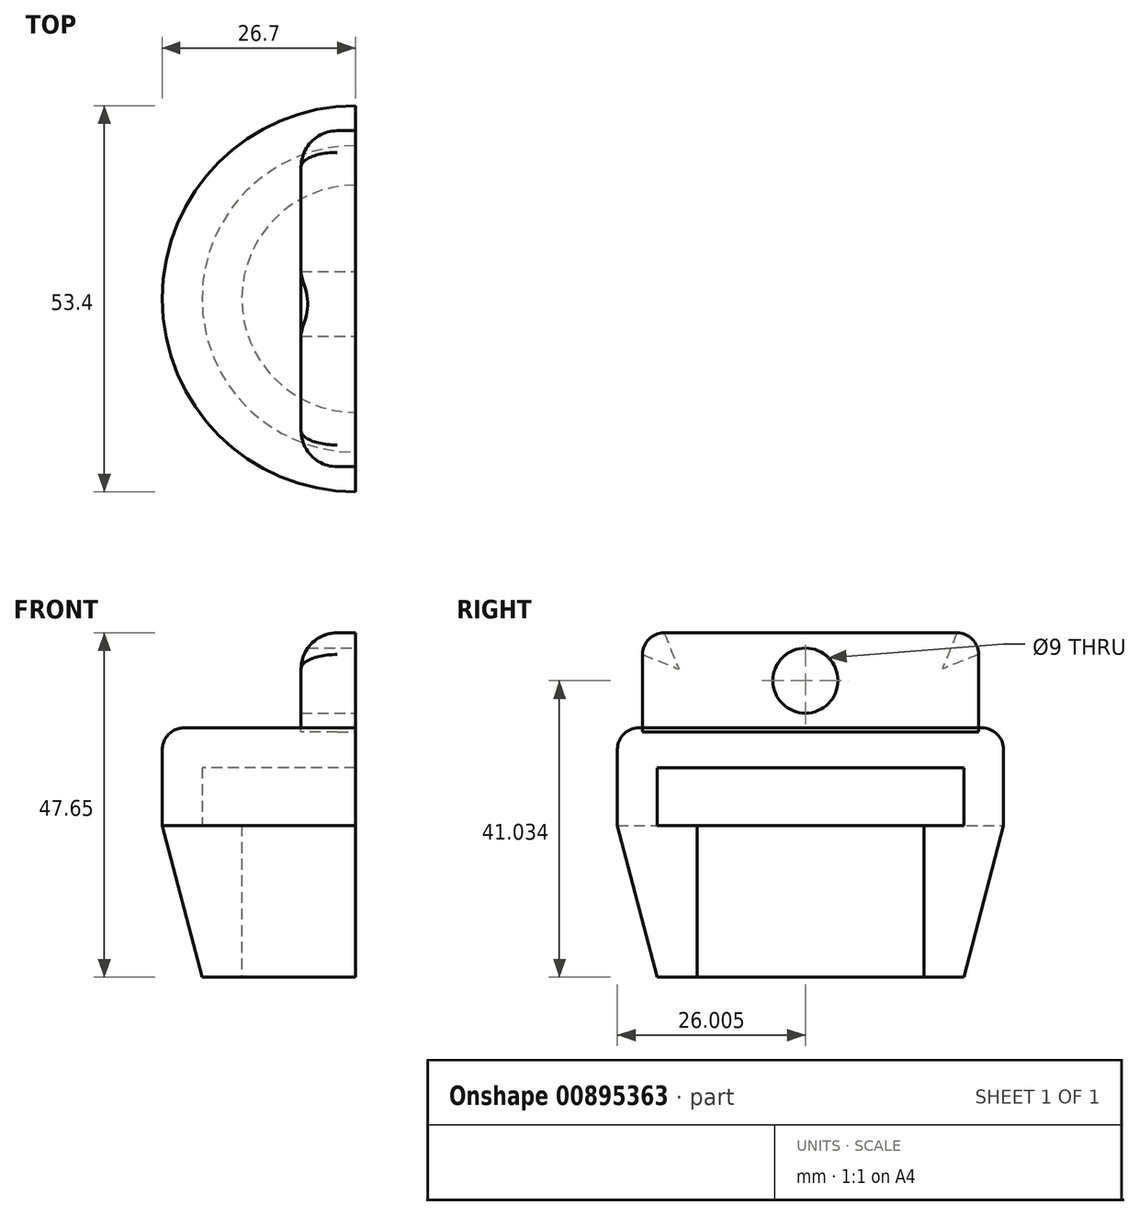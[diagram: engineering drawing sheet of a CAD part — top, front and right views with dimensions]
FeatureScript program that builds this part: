
annotation { "Feature Type Name" : "Feature", "Feature Type Description" : "" }
export const myFeature = defineFeature(function(context is Context, id is Id, definition is map)
    precondition{}
    {
        {
            var Q0;
            Q0=qCreatedBy(makeId("Front.planeOp"),FACE);
            var sketch = newSketch(context, id + "F0", { "sketchPlane" : qUnion([Q0])});
            skPoint(sketch, "E0.end.orphan", {"position": v(0, 30.39) * mm});
            skLineSegment(sketch, "E1", {"start": v(-15.7, 0) * mm, "end": v(-21.2, 0) * mm});
            skLineSegment(sketch, "E2", {"start": v(-15.7, 0) * mm, "end": v(-15.7, 21) * mm});
            skLineSegment(sketch, "E3", {"start": v(-15.7, 21) * mm, "end": v(-21.2, 21) * mm});
            skLineSegment(sketch, "E4", {"start": v(-21.2, 21) * mm, "end": v(-21.2, 29) * mm});
            skLineSegment(sketch, "E5", {"start": v(-26.7, 29) * mm, "end": v(-26.7, 21) * mm});
            skLineSegment(sketch, "E6", {"start": v(-26.7, 21) * mm, "end": v(-21.2, 0) * mm});
            skLineSegment(sketch, "E7", {"start": v(-26.7, 29) * mm, "end": v(-26.7, 34.5) * mm});
            skLineSegment(sketch, "E8", {"start": v(-26.7, 34.5) * mm, "end": v(0, 34.5) * mm});
            skLineSegment(sketch, "E9", {"start": v(-21.2, 29) * mm, "end": v(0, 29) * mm});
            skLineSegment(sketch, "E10", {"start": v(0, 29) * mm, "end": v(0, 34.5) * mm});
            skLineSegment(sketch, "E11", {"start": v(0, 0) * mm, "end": v(0, 6.63) * mm});
            skSolve(sketch);
        }
        {
            var Q0;
            Q0=makeQuery(id+"F0.imprint","IMPRINT",FACE,{"disambiguationData":[TD([[makeQuery(id+"F0.imprint","IMPRINT",EDGE,{"derivedFrom":sQuery(id+"F0.wireOp",EDGE,"E1")}),-1.0]])]});
            var Q1;
            Q1=sQuery(id+"F0.wireOp",EDGE,"E11");
            revolve(context, id + "F1", {"surfaceOperationType" : NewSurfaceOperationType.NEW, "entities" : qUnion([Q0]), "axis" : qUnion([Q1]), "revolveType" : RevolveType.SYMMETRIC, "angle" : 180 * degree});
        }
        {
            var Q0;
            Q0=qCreatedBy(makeId("Right.planeOp"),FACE);
            var sketch = newSketch(context, id + "F2", { "sketchPlane" : qUnion([Q0])});
            skPoint(sketch, "E12.end.orphan", {"position": v(-41.72, 47.65) * mm});
            skPoint(sketch, "E13.end.orphan", {"position": v(-41.72, 21) * mm});
            skLineSegment(sketch, "E14.bottom", {"start": v(23.25, 33.95) * mm, "end": v(-23.23, 33.95) * mm});
            skLineSegment(sketch, "E14.top", {"start": v(23.25, 47.65) * mm, "end": v(-23.23, 47.65) * mm});
            skLineSegment(sketch, "E14.left", {"start": v(23.25, 33.95) * mm, "end": v(23.25, 47.65) * mm});
            skLineSegment(sketch, "E14.right", {"start": v(-23.23, 33.95) * mm, "end": v(-23.23, 47.65) * mm});
            skPoint(sketch, "E15.start.orphan", {"position": v(0, 47.65) * mm});
            skCircle(sketch, "E16", {"center": v(-0.7, 41.03) * mm, "radius": 4.5 * mm});
            skPoint(sketch, "E17.orphan", {"position": v(23.25, 27.87) * mm});
            skSolve(sketch);
        }
        {
            var Q0;
            Q0 = qSketchRegion(id + "F2", true);
            extrude(context, id + "F3", {"entities" : qUnion([Q0]), "depth" : -7.5 * mm, "offsetDistance" : 25 * mm});
        }
        {
            var Q0;
            Q0=makeQuery(id+"F3.opExtrude","SWEPT_EDGE",EDGE,{"disambiguationData":[OSD([sQuery(id+"F2.wireOp",EDGE,"E14.top"),sQuery(id+"F2.wireOp",EDGE,"E14.right")])]});
            var Q1;
            Q1=makeQuery(id+"F3.opExtrude","SWEPT_EDGE",EDGE,{"disambiguationData":[OSD([sQuery(id+"F2.wireOp",EDGE,"E14.top"),sQuery(id+"F2.wireOp",EDGE,"E14.left")])]});
            fillet(context, id + "F4", {"entities" : qUnion([Q0, Q1]), "radius" : 3 * mm, "tangentPropagation" : true, "allowEdgeOverflow" : false});
        }
        {
            var Q0;
            Q0=makeQuery(id+"FytfjTORzdFREBd_2.opPattern","COPY",EDGE,{"derivedFrom":makeQuery(id+"F1.opRevolve","SWEPT_EDGE",EDGE,{"disambiguationData":[OSD([sQuery(id+"F0.wireOp",EDGE,"E7"),sQuery(id+"F0.wireOp",EDGE,"E8")])]}),"instanceName":"1"});
            var Q1;
            Q1=makeQuery(id+"F1.opRevolve","SWEPT_EDGE",EDGE,{"disambiguationData":[OSD([sQuery(id+"F0.wireOp",EDGE,"E7"),sQuery(id+"F0.wireOp",EDGE,"E8")])]});
            fillet(context, id + "F5", {"entities" : qUnion([Q0, Q1]), "radius" : 3 * mm, "tangentPropagation" : true, "allowEdgeOverflow" : false});
        }
        {
            var Q0;
            Q0=makeQuery(id+"F3.opExtrude","CAP_EDGE",EDGE,{"disambiguationData":[OSD([sQuery(id+"F2.wireOp",EDGE,"E14.right")])],"isStart":false});
            fillet(context, id + "F6", {"entities" : qUnion([Q0]), "radius" : 5 * mm, "tangentPropagation" : true, "allowEdgeOverflow" : false});
        }
    });
